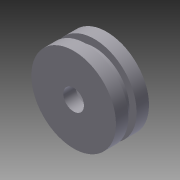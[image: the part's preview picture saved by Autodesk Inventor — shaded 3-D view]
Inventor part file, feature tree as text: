
AUTODESK INVENTOR PART (.ipt)
format: ipt  version: 2011 (Build 150229000, 229)  size: 99,840 bytes
history: native  units: mm
features: revolve x1, sketch x1
ambient origin geometry x8: Origin, YZ Plane, XZ Plane, XY Plane, X Axis, Y Axis, Z Axis, Center Point
feature tree (2):
  revolve  "Revolution1"  [1 undecoded]
  sketch  "Sketch1"  dims[d0=10.0mm d1=26.0mm d2=34.0mm d3=41.0mm d4=6.0mm d5=10.0mm d6=16.0mm d7=90.0deg]
note: 1 required parameter value undecoded (feature->parameter linkage not recoverable at this tier; creation-order binding heuristic only, values carry confidence <= 0.55)
